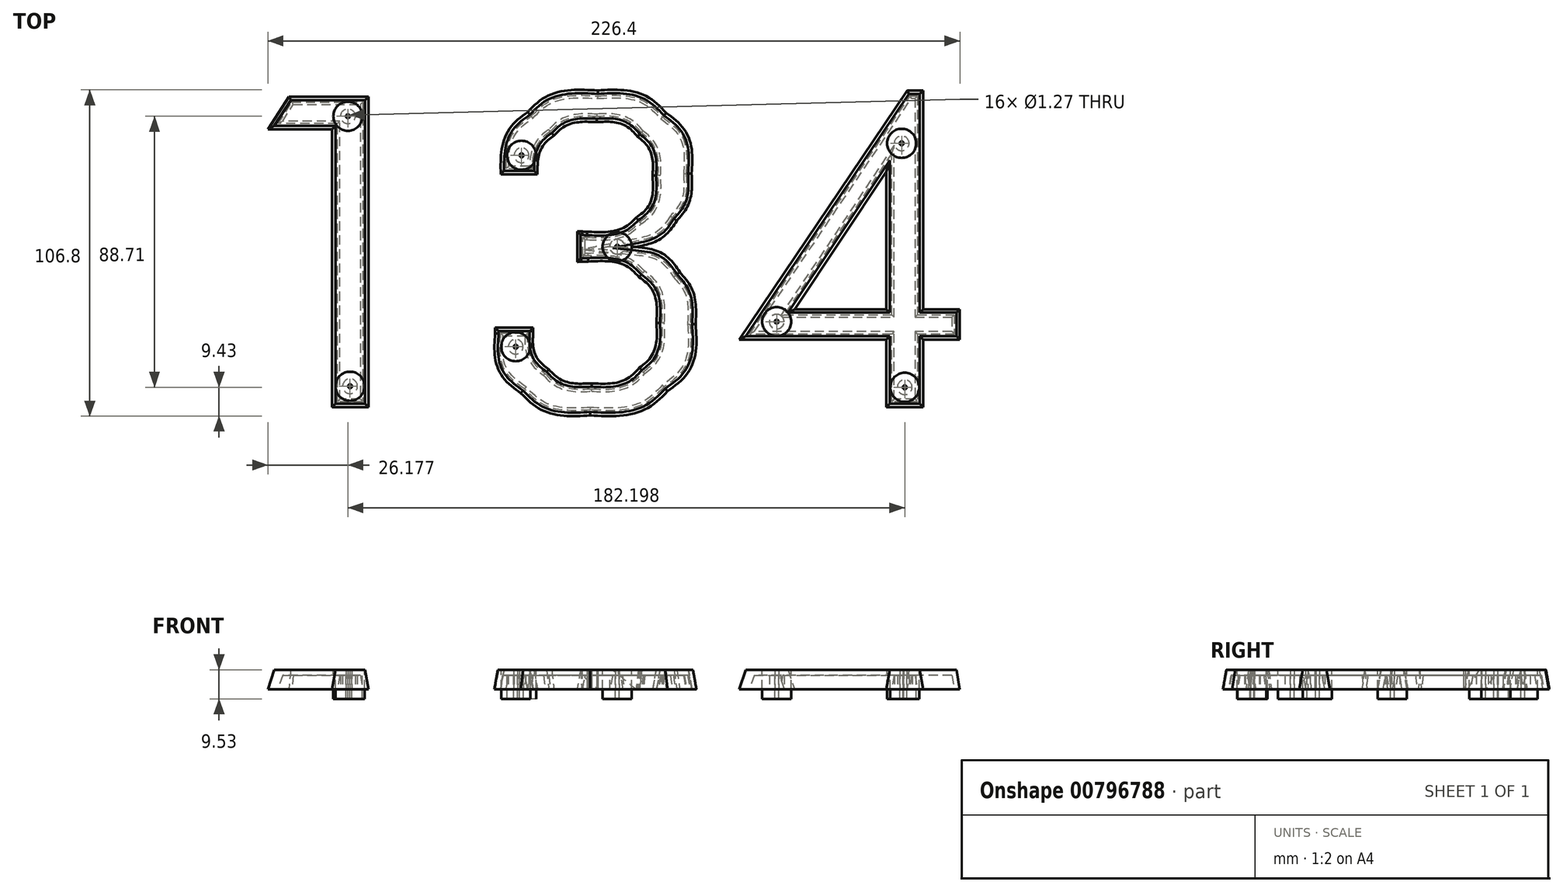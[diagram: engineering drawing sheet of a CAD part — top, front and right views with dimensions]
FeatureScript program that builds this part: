
annotation { "Feature Type Name" : "Feature", "Feature Type Description" : "" }
export const myFeature = defineFeature(function(context is Context, id is Id, definition is map)
    precondition{}
    {
        {
            var Q0;
            Q0=qCreatedBy(makeId("Top.planeOp"),FACE);
            var sketch = newSketch(context, id + "F0", { "sketchPlane" : qUnion([Q0])});
            skLineSegment(sketch, "E0", {"start": v(-92.25, -50.45) * mm, "end": v(-92.25, 40.5) * mm});
            skLineSegment(sketch, "E1", {"start": v(-92.25, 40.5) * mm, "end": v(-113.2, 40.5) * mm});
            skLineSegment(sketch, "E2", {"start": v(-113.2, 40.5) * mm, "end": v(-106.33, 51.15) * mm});
            skLineSegment(sketch, "E3", {"start": v(-106.33, 51.15) * mm, "end": v(-80.33, 51.15) * mm});
            skLineSegment(sketch, "E4", {"start": v(-80.33, 51.15) * mm, "end": v(-80.33, -50.45) * mm});
            skLineSegment(sketch, "E5", {"start": v(-80.33, -50.45) * mm, "end": v(-92.25, -50.45) * mm});
            skFitSpline(sketch, "E6", {"points": [v(-26.38, -25.65) * mm, v(-26.38, -30.88) * mm, v(-24.68, -35.03) * mm, v(-21.27, -38.12) * mm]});
            skFitSpline(sketch, "E7", {"points": [v(-21.27, -38.12) * mm, v(-17.86, -41.15) * mm, v(-13.2, -42.67) * mm, v(-7.32, -42.67) * mm]});
            skFitSpline(sketch, "E8", {"points": [v(-7.32, -42.67) * mm, v(-0.55, -42.67) * mm, v(4.68, -40.97) * mm, v(8.37, -37.56) * mm]});
            skFitSpline(sketch, "E9", {"points": [v(8.37, -37.56) * mm, v(12.06, -34.1) * mm, v(13.9, -29.22) * mm, v(13.9, -22.91) * mm]});
            skFitSpline(sketch, "E10", {"points": [v(13.9, -22.91) * mm, v(13.9, -16.28) * mm, v(12.02, -11.28) * mm, v(8.23, -7.92) * mm]});
            skFitSpline(sketch, "E11", {"points": [v(8.23, -7.92) * mm, v(4.5, -4.5) * mm, v(-1.06, -2.8) * mm, v(-8.44, -2.8) * mm]});
            skFitSpline(sketch, "E12", {"points": [v(-8.44, -2.8) * mm, v(-9.38, -2.8) * mm, v(-10.1, -2.83) * mm, v(-10.62, -2.87) * mm]});
            skFitSpline(sketch, "E13", {"points": [v(-10.62, -2.87) * mm, v(-11.08, -2.87) * mm, v(-11.55, -2.9) * mm, v(-12.02, -2.94) * mm]});
            skLineSegment(sketch, "E14", {"start": v(-38.85, -24.45) * mm, "end": v(-26.38, -24.45) * mm});
            skLineSegment(sketch, "E15", {"start": v(-26.38, -24.45) * mm, "end": v(-26.38, -25.65) * mm});
            skFitSpline(sketch, "E16", {"points": [v(-12.02, 7.08) * mm, v(-11.64, 7.08) * mm, v(-11.1, 7.05) * mm, v(-10.4, 7) * mm]});
            skFitSpline(sketch, "E17", {"points": [v(-10.4, 7) * mm, v(-9.66, 6.96) * mm, v(-9.1, 6.94) * mm, v(-8.72, 6.94) * mm]});
            skFitSpline(sketch, "E18", {"points": [v(-8.72, 6.94) * mm, v(-1.67, 6.94) * mm, v(3.66, 8.48) * mm, v(7.25, 11.56) * mm]});
            skFitSpline(sketch, "E19", {"points": [v(7.25, 11.56) * mm, v(10.85, 14.64) * mm, v(12.65, 19.22) * mm, v(12.65, 25.3) * mm]});
            skFitSpline(sketch, "E20", {"points": [v(12.65, 25.3) * mm, v(12.65, 30.67) * mm, v(11.01, 34.92) * mm, v(7.74, 38.05) * mm]});
            skFitSpline(sketch, "E21", {"points": [v(7.74, 38.05) * mm, v(4.47, 41.22) * mm, v(0.04, 42.81) * mm, v(-5.57, 42.81) * mm]});
            skFitSpline(sketch, "E22", {"points": [v(-5.57, 42.81) * mm, v(-11.55, 42.81) * mm, v(-16.22, 41.34) * mm, v(-19.58, 38.4) * mm]});
            skFitSpline(sketch, "E23", {"points": [v(-19.58, 38.4) * mm, v(-22.9, 35.5) * mm, v(-24.7, 31.27) * mm, v(-24.98, 25.72) * mm]});
            skLineSegment(sketch, "E24", {"start": v(-12.02, -2.94) * mm, "end": v(-12.02, 7.08) * mm});
            skLineSegment(sketch, "E25", {"start": v(-12.02, 7.08) * mm, "end": v(-12.02, -2.94) * mm});
            skFitSpline(sketch, "E26", {"points": [v(-37.03, 25.79) * mm, v(-36.56, 34.61) * mm, v(-33.62, 41.39) * mm, v(-28.2, 46.1) * mm]});
            skFitSpline(sketch, "E27", {"points": [v(-28.2, 46.1) * mm, v(-22.74, 50.82) * mm, v(-15.1, 53.18) * mm, v(-5.3, 53.18) * mm]});
            skFitSpline(sketch, "E28", {"points": [v(-5.3, 53.18) * mm, v(4.15, 53.18) * mm, v(11.62, 50.73) * mm, v(17.13, 45.83) * mm]});
            skFitSpline(sketch, "E29", {"points": [v(17.13, 45.83) * mm, v(22.64, 40.92) * mm, v(25.4, 34.29) * mm, v(25.4, 25.93) * mm]});
            skFitSpline(sketch, "E30", {"points": [v(25.4, 25.93) * mm, v(25.4, 19.85) * mm, v(23.79, 14.71) * mm, v(20.57, 10.51) * mm]});
            skFitSpline(sketch, "E31", {"points": [v(20.57, 10.51) * mm, v(17.39, 6.3) * mm, v(12.93, 3.46) * mm, v(7.18, 1.96) * mm]});
            skFitSpline(sketch, "E32", {"points": [v(7.18, 1.96) * mm, v(13.3, 0.93) * mm, v(18.09, -1.82) * mm, v(21.55, -6.3) * mm]});
            skFitSpline(sketch, "E33", {"points": [v(21.55, -6.3) * mm, v(25, -10.74) * mm, v(26.73, -16.42) * mm, v(26.73, -23.33) * mm]});
            skFitSpline(sketch, "E34", {"points": [v(26.73, -23.33) * mm, v(26.73, -32.63) * mm, v(23.67, -39.94) * mm, v(17.55, -45.26) * mm]});
            skFitSpline(sketch, "E35", {"points": [v(17.55, -45.26) * mm, v(11.48, -50.54) * mm, v(3.05, -53.18) * mm, v(-7.74, -53.18) * mm]});
            skFitSpline(sketch, "E36", {"points": [v(-7.74, -53.18) * mm, v(-17.23, -53.18) * mm, v(-24.8, -50.75) * mm, v(-30.44, -45.9) * mm]});
            skFitSpline(sketch, "E37", {"points": [v(-30.44, -45.9) * mm, v(-36.05, -41.04) * mm, v(-38.85, -34.52) * mm, v(-38.85, -26.35) * mm]});
            skLineSegment(sketch, "E38", {"start": v(-24.98, 25.72) * mm, "end": v(-37.03, 25.79) * mm});
            skLineSegment(sketch, "E39", {"start": v(-37.03, 25.79) * mm, "end": v(-24.98, 25.72) * mm});
            skLineSegment(sketch, "E40", {"start": v(-38.85, -26.35) * mm, "end": v(-38.85, -24.45) * mm});
            skLineSegment(sketch, "E41", {"start": v(-38.85, -24.45) * mm, "end": v(-38.85, -24.45) * mm});
            skLineSegment(sketch, "E42", {"start": v(-38.85, -24.45) * mm, "end": v(-38.85, -26.35) * mm});
            skLineSegment(sketch, "E43", {"start": v(89.1, -50.45) * mm, "end": v(89.1, -28.38) * mm});
            skLineSegment(sketch, "E44", {"start": v(89.1, -28.38) * mm, "end": v(41.03, -28.38) * mm});
            skLineSegment(sketch, "E45", {"start": v(41.03, -28.38) * mm, "end": v(95.96, 53.18) * mm});
            skLineSegment(sketch, "E46", {"start": v(95.96, 53.18) * mm, "end": v(101.14, 53.18) * mm});
            skLineSegment(sketch, "E47", {"start": v(101.14, 53.18) * mm, "end": v(101.14, -18.43) * mm});
            skLineSegment(sketch, "E48", {"start": v(101.14, -18.43) * mm, "end": v(113.2, -18.43) * mm});
            skLineSegment(sketch, "E49", {"start": v(113.2, -18.43) * mm, "end": v(113.2, -28.38) * mm});
            skLineSegment(sketch, "E50", {"start": v(113.2, -28.38) * mm, "end": v(101.14, -28.38) * mm});
            skLineSegment(sketch, "E51", {"start": v(101.14, -28.38) * mm, "end": v(101.14, -50.45) * mm});
            skLineSegment(sketch, "E52", {"start": v(101.14, -50.45) * mm, "end": v(89.1, -50.45) * mm});
            skLineSegment(sketch, "E53", {"start": v(89.1, -18.43) * mm, "end": v(89.1, 26.63) * mm});
            skLineSegment(sketch, "E54", {"start": v(89.1, 26.63) * mm, "end": v(59.1, -18.43) * mm});
            skLineSegment(sketch, "E55", {"start": v(59.1, -18.43) * mm, "end": v(89.1, -18.43) * mm});
            skCircle(sketch, "E56", {"center": v(94.16, 35.88) * mm, "radius": 4.76 * mm});
            skCircle(sketch, "E57", {"center": v(94.16, 35.88) * mm, "radius": 0.64 * mm});
            skCircle(sketch, "E58", {"center": v(1.09, 2.03) * mm, "radius": 4.76 * mm});
            skCircle(sketch, "E59", {"center": v(1.09, 2.03) * mm, "radius": 0.64 * mm});
            skCircle(sketch, "E60", {"center": v(-30.2, 31.95) * mm, "radius": 4.76 * mm});
            skCircle(sketch, "E61", {"center": v(-30.2, 31.95) * mm, "radius": 0.64 * mm});
            skCircle(sketch, "E62", {"center": v(-32.12, -30.7) * mm, "radius": 4.76 * mm});
            skCircle(sketch, "E63", {"center": v(-32.12, -30.7) * mm, "radius": 0.64 * mm});
            skCircle(sketch, "E64", {"center": v(-87.02, 44.73) * mm, "radius": 4.76 * mm});
            skCircle(sketch, "E65", {"center": v(-87.02, 44.73) * mm, "radius": 0.64 * mm});
            skCircle(sketch, "E66", {"center": v(-86.33, -43.62) * mm, "radius": 4.76 * mm});
            skCircle(sketch, "E67", {"center": v(-86.33, -43.62) * mm, "radius": 0.64 * mm});
            skCircle(sketch, "E68", {"center": v(53.27, -22.48) * mm, "radius": 4.76 * mm});
            skCircle(sketch, "E69", {"center": v(53.27, -22.48) * mm, "radius": 0.64 * mm});
            skCircle(sketch, "E70", {"center": v(95.18, -43.98) * mm, "radius": 4.76 * mm});
            skCircle(sketch, "E71", {"center": v(95.18, -43.98) * mm, "radius": 0.64 * mm});
            skSolve(sketch);
        }
        {
            var Q0;
            Q0=makeQuery(id+"F0.imprint","IMPRINT",FACE,{"disambiguationData":[TD([[makeQuery(id+"F0.imprint","IMPRINT",EDGE,{"derivedFrom":sQuery(id+"F0.wireOp",EDGE,"E0")}),-1.0]])]});
            var Q1;
            Q1=makeQuery(id+"F0.imprint","IMPRINT",FACE,{"disambiguationData":[TD([[makeQuery(id+"F0.imprint","IMPRINT",EDGE,{"derivedFrom":sQuery(id+"F0.wireOp",EDGE,"E6")}),-1.0]])]});
            var Q2;
            Q2=makeQuery(id+"F0.imprint","IMPRINT",FACE,{"disambiguationData":[TD([[makeQuery(id+"F0.imprint","IMPRINT",EDGE,{"derivedFrom":sQuery(id+"F0.wireOp",EDGE,"E43")}),-1.0]])]});
            var Q3;
            Q3=makeQuery(id+"F0.imprint","IMPRINT",FACE,{"disambiguationData":[TD([[makeQuery(id+"F0.imprint","IMPRINT",EDGE,{"derivedFrom":sQuery(id+"F0.wireOp",EDGE,"E56")}),1.0]])]});
            var Q4;
            Q4=makeQuery(id+"F0.imprint","IMPRINT",FACE,{"disambiguationData":[TD([[makeQuery(id+"F0.imprint","IMPRINT",EDGE,{"derivedFrom":sQuery(id+"F0.wireOp",EDGE,"E70")}),1.0]])]});
            var Q5;
            Q5=makeQuery(id+"F0.imprint","IMPRINT",FACE,{"disambiguationData":[TD([[makeQuery(id+"F0.imprint","IMPRINT",EDGE,{"derivedFrom":sQuery(id+"F0.wireOp",EDGE,"E58")}),1.0]])]});
            var Q6;
            Q6=makeQuery(id+"F0.imprint","IMPRINT",FACE,{"disambiguationData":[TD([[makeQuery(id+"F0.imprint","IMPRINT",EDGE,{"derivedFrom":sQuery(id+"F0.wireOp",EDGE,"E62")}),1.0]])]});
            var Q7;
            Q7=makeQuery(id+"F0.imprint","IMPRINT",FACE,{"disambiguationData":[TD([[makeQuery(id+"F0.imprint","IMPRINT",EDGE,{"derivedFrom":sQuery(id+"F0.wireOp",EDGE,"E68")}),1.0]])]});
            var Q8;
            Q8=makeQuery(id+"F0.imprint","IMPRINT",FACE,{"disambiguationData":[TD([[makeQuery(id+"F0.imprint","IMPRINT",EDGE,{"derivedFrom":sQuery(id+"F0.wireOp",EDGE,"E66")}),1.0]])]});
            var Q9;
            Q9=makeQuery(id+"F0.imprint","IMPRINT",FACE,{"disambiguationData":[TD([[makeQuery(id+"F0.imprint","IMPRINT",EDGE,{"derivedFrom":sQuery(id+"F0.wireOp",EDGE,"E67")}),1.0]])]});
            var Q10;
            Q10=makeQuery(id+"F0.imprint","IMPRINT",FACE,{"disambiguationData":[TD([[makeQuery(id+"F0.imprint","IMPRINT",EDGE,{"derivedFrom":sQuery(id+"F0.wireOp",EDGE,"E63")}),1.0]])]});
            var Q11;
            Q11=makeQuery(id+"F0.imprint","IMPRINT",FACE,{"disambiguationData":[TD([[makeQuery(id+"F0.imprint","IMPRINT",EDGE,{"derivedFrom":sQuery(id+"F0.wireOp",EDGE,"E59")}),1.0]])]});
            var Q12;
            Q12=makeQuery(id+"F0.imprint","IMPRINT",FACE,{"disambiguationData":[TD([[makeQuery(id+"F0.imprint","IMPRINT",EDGE,{"derivedFrom":sQuery(id+"F0.wireOp",EDGE,"E60")}),1.0]])]});
            var Q13;
            Q13=makeQuery(id+"F0.imprint","IMPRINT",FACE,{"disambiguationData":[TD([[makeQuery(id+"F0.imprint","IMPRINT",EDGE,{"derivedFrom":sQuery(id+"F0.wireOp",EDGE,"E61")}),1.0]])]});
            var Q14;
            Q14=makeQuery(id+"F0.imprint","IMPRINT",FACE,{"disambiguationData":[TD([[makeQuery(id+"F0.imprint","IMPRINT",EDGE,{"derivedFrom":sQuery(id+"F0.wireOp",EDGE,"E69")}),1.0]])]});
            var Q15;
            Q15=makeQuery(id+"F0.imprint","IMPRINT",FACE,{"disambiguationData":[TD([[makeQuery(id+"F0.imprint","IMPRINT",EDGE,{"derivedFrom":sQuery(id+"F0.wireOp",EDGE,"E71")}),1.0]])]});
            var Q16;
            Q16=makeQuery(id+"F0.imprint","IMPRINT",FACE,{"disambiguationData":[TD([[makeQuery(id+"F0.imprint","IMPRINT",EDGE,{"derivedFrom":sQuery(id+"F0.wireOp",EDGE,"E57")}),1.0]])]});
            var Q17;
            Q17=makeQuery(id+"F0.imprint","IMPRINT",FACE,{"disambiguationData":[TD([[makeQuery(id+"F0.imprint","IMPRINT",EDGE,{"derivedFrom":sQuery(id+"F0.wireOp",EDGE,"E65")}),1.0]])]});
            var Q18;
            Q18=makeQuery(id+"F0.imprint","IMPRINT",FACE,{"disambiguationData":[TD([[makeQuery(id+"F0.imprint","IMPRINT",EDGE,{"derivedFrom":sQuery(id+"F0.wireOp",EDGE,"E64")}),1.0]])]});
            extrude(context, id + "F1", {"entities" : qUnion([Q0, Q1, Q2, Q3, Q4, Q5, Q6, Q7, Q8, Q9, Q10, Q11, Q12, Q13, Q14, Q15, Q16, Q17, Q18]), "depth" : 6.35 * mm, "offsetDistance" : 25.4 * mm, "hasDraft" : true, "draftAngle" : 10 * degree, "draftPullDirection" : true});
        }
        {
            var Q0;
            Q0=makeQuery(id+"F0.imprint","IMPRINT",FACE,{"disambiguationData":[TD([[makeQuery(id+"F0.imprint","IMPRINT",EDGE,{"derivedFrom":sQuery(id+"F0.wireOp",EDGE,"E56")}),1.0]])]});
            var Q1;
            Q1=makeQuery(id+"F0.imprint","IMPRINT",FACE,{"disambiguationData":[TD([[makeQuery(id+"F0.imprint","IMPRINT",EDGE,{"derivedFrom":sQuery(id+"F0.wireOp",EDGE,"E68")}),1.0]])]});
            var Q2;
            Q2=makeQuery(id+"F0.imprint","IMPRINT",FACE,{"disambiguationData":[TD([[makeQuery(id+"F0.imprint","IMPRINT",EDGE,{"derivedFrom":sQuery(id+"F0.wireOp",EDGE,"E70")}),1.0]])]});
            var Q3;
            Q3=makeQuery(id+"F0.imprint","IMPRINT",FACE,{"disambiguationData":[TD([[makeQuery(id+"F0.imprint","IMPRINT",EDGE,{"derivedFrom":sQuery(id+"F0.wireOp",EDGE,"E58")}),1.0]])]});
            var Q4;
            Q4=makeQuery(id+"F0.imprint","IMPRINT",FACE,{"disambiguationData":[TD([[makeQuery(id+"F0.imprint","IMPRINT",EDGE,{"derivedFrom":sQuery(id+"F0.wireOp",EDGE,"E62")}),1.0]])]});
            var Q5;
            Q5=makeQuery(id+"F0.imprint","IMPRINT",FACE,{"disambiguationData":[TD([[makeQuery(id+"F0.imprint","IMPRINT",EDGE,{"derivedFrom":sQuery(id+"F0.wireOp",EDGE,"E60")}),1.0]])]});
            var Q6;
            Q6=makeQuery(id+"F0.imprint","IMPRINT",FACE,{"disambiguationData":[TD([[makeQuery(id+"F0.imprint","IMPRINT",EDGE,{"derivedFrom":sQuery(id+"F0.wireOp",EDGE,"E64")}),1.0]])]});
            var Q7;
            Q7=makeQuery(id+"F0.imprint","IMPRINT",FACE,{"disambiguationData":[TD([[makeQuery(id+"F0.imprint","IMPRINT",EDGE,{"derivedFrom":sQuery(id+"F0.wireOp",EDGE,"E66")}),1.0]])]});
            extrude(context, id + "F2", {"entities" : qUnion([Q0, Q1, Q2, Q3, Q4, Q5, Q6, Q7]), "oppositeDirection" : true, "depth" : 3.17 * mm, "offsetDistance" : 25.4 * mm, "hasSecondDirection" : true, "secondDirectionOppositeDirection" : false, "secondDirectionDepth" : 6.35 * mm});
        }
        {
            var Q0;
            Q0=makeQuery(id+"F0.imprint","IMPRINT",FACE,{"disambiguationData":[TD([[makeQuery(id+"F0.imprint","IMPRINT",EDGE,{"derivedFrom":sQuery(id+"F0.wireOp",EDGE,"E71")}),1.0]])]});
            var Q1;
            Q1=makeQuery(id+"F0.imprint","IMPRINT",FACE,{"disambiguationData":[TD([[makeQuery(id+"F0.imprint","IMPRINT",EDGE,{"derivedFrom":sQuery(id+"F0.wireOp",EDGE,"E69")}),1.0]])]});
            var Q2;
            Q2=makeQuery(id+"F0.imprint","IMPRINT",FACE,{"disambiguationData":[TD([[makeQuery(id+"F0.imprint","IMPRINT",EDGE,{"derivedFrom":sQuery(id+"F0.wireOp",EDGE,"E57")}),1.0]])]});
            var Q3;
            Q3=makeQuery(id+"F0.imprint","IMPRINT",FACE,{"disambiguationData":[TD([[makeQuery(id+"F0.imprint","IMPRINT",EDGE,{"derivedFrom":sQuery(id+"F0.wireOp",EDGE,"E59")}),1.0]])]});
            var Q4;
            Q4=makeQuery(id+"F0.imprint","IMPRINT",FACE,{"disambiguationData":[TD([[makeQuery(id+"F0.imprint","IMPRINT",EDGE,{"derivedFrom":sQuery(id+"F0.wireOp",EDGE,"E63")}),1.0]])]});
            var Q5;
            Q5=makeQuery(id+"F0.imprint","IMPRINT",FACE,{"disambiguationData":[TD([[makeQuery(id+"F0.imprint","IMPRINT",EDGE,{"derivedFrom":sQuery(id+"F0.wireOp",EDGE,"E61")}),1.0]])]});
            var Q6;
            Q6=makeQuery(id+"F0.imprint","IMPRINT",FACE,{"disambiguationData":[TD([[makeQuery(id+"F0.imprint","IMPRINT",EDGE,{"derivedFrom":sQuery(id+"F0.wireOp",EDGE,"E67")}),1.0]])]});
            var Q7;
            Q7=makeQuery(id+"F0.imprint","IMPRINT",FACE,{"disambiguationData":[TD([[makeQuery(id+"F0.imprint","IMPRINT",EDGE,{"derivedFrom":sQuery(id+"F0.wireOp",EDGE,"E65")}),1.0]])]});
            extrude(context, id + "F3", {"entities" : qUnion([Q0, Q1, Q2, Q3, Q4, Q5, Q6, Q7]), "operationType" : NewBodyOperationType.REMOVE, "endBound" : BoundingType.THROUGH_ALL, "depth" : 25.4 * mm, "offsetDistance" : 25.4 * mm});
        }
        {
            var Q0;
            Q0=makeQuery(id+"F1.opExtrude","CAP_FACE",FACE,{"disambiguationData":[OSD([sQuery(id+"F0.wireOp",EDGE,"E43"),sQuery(id+"F0.wireOp",EDGE,"E44"),sQuery(id+"F0.wireOp",EDGE,"E45"),sQuery(id+"F0.wireOp",EDGE,"E46"),sQuery(id+"F0.wireOp",EDGE,"E47"),sQuery(id+"F0.wireOp",EDGE,"E48"),sQuery(id+"F0.wireOp",EDGE,"E49"),sQuery(id+"F0.wireOp",EDGE,"E50"),sQuery(id+"F0.wireOp",EDGE,"E51"),sQuery(id+"F0.wireOp",EDGE,"E52"),sQuery(id+"F0.wireOp",EDGE,"E53"),sQuery(id+"F0.wireOp",EDGE,"E54"),sQuery(id+"F0.wireOp",EDGE,"E55")])],"isStart":true});
            var Q1;
            Q1=makeQuery(id+"F1.opExtrude","CAP_FACE",FACE,{"disambiguationData":[OSD([sQuery(id+"F0.wireOp",EDGE,"E6"),sQuery(id+"F0.wireOp",EDGE,"E7"),sQuery(id+"F0.wireOp",EDGE,"E8"),sQuery(id+"F0.wireOp",EDGE,"E9"),sQuery(id+"F0.wireOp",EDGE,"E10"),sQuery(id+"F0.wireOp",EDGE,"E11"),sQuery(id+"F0.wireOp",EDGE,"E12"),sQuery(id+"F0.wireOp",EDGE,"E13"),sQuery(id+"F0.wireOp",EDGE,"E14"),sQuery(id+"F0.wireOp",EDGE,"E15"),sQuery(id+"F0.wireOp",EDGE,"E16"),sQuery(id+"F0.wireOp",EDGE,"E17"),sQuery(id+"F0.wireOp",EDGE,"E18"),sQuery(id+"F0.wireOp",EDGE,"E19"),sQuery(id+"F0.wireOp",EDGE,"E20"),sQuery(id+"F0.wireOp",EDGE,"E21"),sQuery(id+"F0.wireOp",EDGE,"E22"),sQuery(id+"F0.wireOp",EDGE,"E23"),sQuery(id+"F0.wireOp",EDGE,"E25"),sQuery(id+"F0.wireOp",EDGE,"E26"),sQuery(id+"F0.wireOp",EDGE,"E27"),sQuery(id+"F0.wireOp",EDGE,"E28"),sQuery(id+"F0.wireOp",EDGE,"E29"),sQuery(id+"F0.wireOp",EDGE,"E30"),sQuery(id+"F0.wireOp",EDGE,"E31"),sQuery(id+"F0.wireOp",EDGE,"E32"),sQuery(id+"F0.wireOp",EDGE,"E33"),sQuery(id+"F0.wireOp",EDGE,"E34"),sQuery(id+"F0.wireOp",EDGE,"E35"),sQuery(id+"F0.wireOp",EDGE,"E36"),sQuery(id+"F0.wireOp",EDGE,"E37"),sQuery(id+"F0.wireOp",EDGE,"E39"),sQuery(id+"F0.wireOp",EDGE,"E42")])],"isStart":true});
            var Q2;
            Q2=makeQuery(id+"F1.opExtrude","CAP_FACE",FACE,{"disambiguationData":[OSD([sQuery(id+"F0.wireOp",EDGE,"E0"),sQuery(id+"F0.wireOp",EDGE,"E1"),sQuery(id+"F0.wireOp",EDGE,"E2"),sQuery(id+"F0.wireOp",EDGE,"E3"),sQuery(id+"F0.wireOp",EDGE,"E4"),sQuery(id+"F0.wireOp",EDGE,"E5")])],"isStart":true});
            shell(context, id + "F4", {"entities" : qUnion([Q0, Q1, Q2]), "thickness" : 1.78 * mm});
        }
    });
